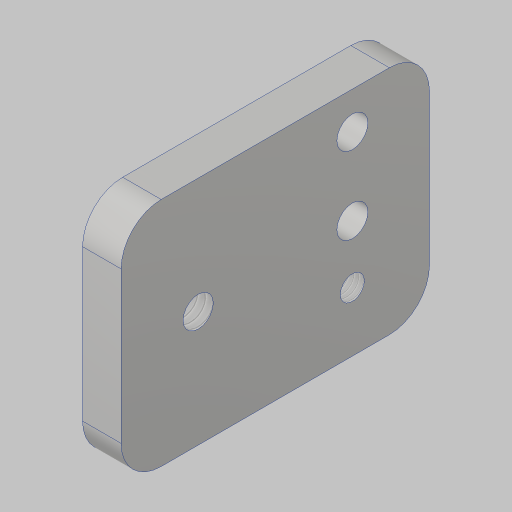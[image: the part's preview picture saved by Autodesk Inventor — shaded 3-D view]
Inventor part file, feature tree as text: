
AUTODESK INVENTOR PART (.ipt)
format: ipt  version: 2023.5 (Build 275446000, 446)  size: 128,512 bytes
history: native  units: in
note: dims shown in document units (in); Inventor stores cm internally (conversion verified against a paired STEP export)
features: sketch x3, hole x3, extrude x1, fillet x1
ambient origin geometry x8: Origin, YZ Plane, XZ Plane, XY Plane, X Axis, Y Axis, Z Axis, Center Point
bodies: Solid1 (feature_tree)
feature tree (8):
  extrude  "Extrusion1"  Depth=2.0in
  sketch  "Sketch2"  dims[d2=0.25in d3=0.0in d4=0.5in]
  hole  "Hole1"  [1 undecoded]
  hole  "Hole2"  [1 undecoded]
  hole  "Hole3"  [1 undecoded]
  fillet  "Fillet1"  Radius=0.5in
  sketch  "Sketch1"  dims[d0=1.5in d1=2.0in]
  sketch  "Sketch3"  dims[d5=0.375in d6=0.24in d7=0.5in d8=0.201in d9=0.75in d10=0.385in d11=0.25in d12=0.5635in d13=1.0in d14=0.8108in d15=0.156in d16=0.38in d17=0.375in d18=0.25in d19=0.5635in d20=1.0in d21=0.8108in d22=0.5in d23=0.196in d24=0.5in d25=0.375in d26=0.25in d27=0.5635in d28=1.0in d29=0.8108in d30=0.26in]
note: 3 required parameter values undecoded (feature->parameter linkage not recoverable at this tier; creation-order binding heuristic only, values carry confidence <= 0.55)
